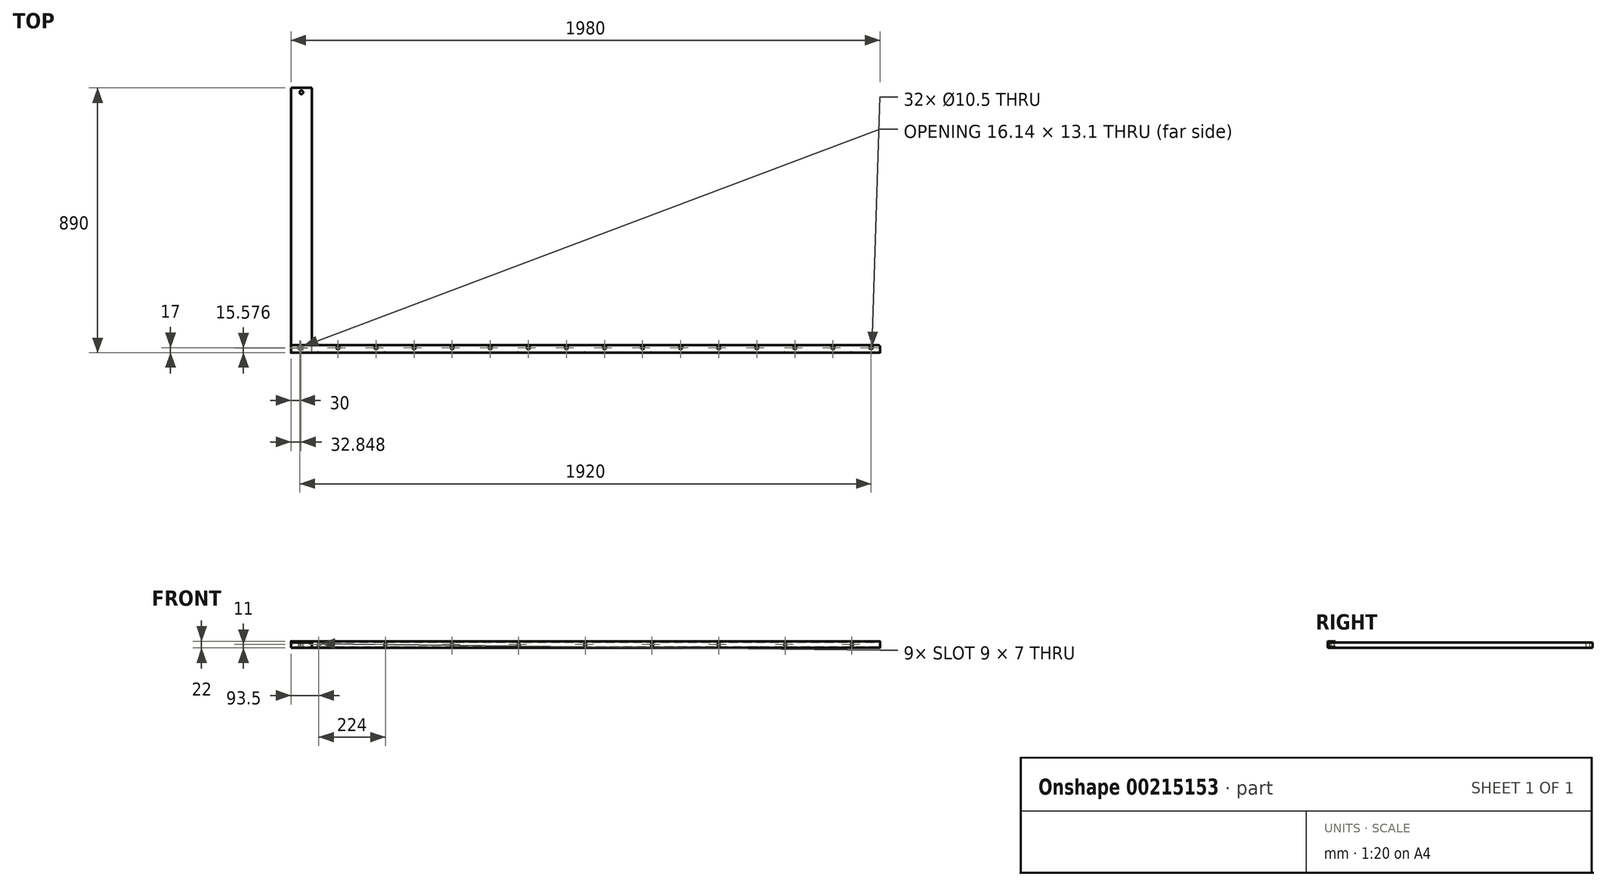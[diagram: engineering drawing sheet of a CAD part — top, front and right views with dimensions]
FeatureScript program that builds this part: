
annotation { "Feature Type Name" : "Feature", "Feature Type Description" : "" }
export const myFeature = defineFeature(function(context is Context, id is Id, definition is map)
    precondition{}
    {
        {
            var Q0;
            Q0=qCreatedBy(makeId("Top.planeOp"),FACE);
            var sketch = newSketch(context, id + "F0", { "sketchPlane" : qUnion([Q0])});
            skLineSegment(sketch, "E0.bottom", {"start": v(0, 0) * mm, "end": v(70, 0) * mm});
            skLineSegment(sketch, "E0.top", {"start": v(0, 890) * mm, "end": v(70, 890) * mm});
            skLineSegment(sketch, "E0.left", {"start": v(0, 0) * mm, "end": v(0, 890) * mm});
            skLineSegment(sketch, "E0.right", {"start": v(70, 0) * mm, "end": v(70, 890) * mm});
            skSolve(sketch);
        }
        {
            var Q0;
            Q0 = qSketchRegion(id + "F0", true);
            extrude(context, id + "F1", {"entities" : qUnion([Q0]), "depth" : 18 * mm});
        }
        {
            var Q0;
            Q0=makeQuery(id+"F1.opExtrude","CAP_FACE",FACE,{"disambiguationData":[OSD([sQuery(id+"F0.wireOp",EDGE,"E0.bottom"),sQuery(id+"F0.wireOp",EDGE,"E0.top"),sQuery(id+"F0.wireOp",EDGE,"E0.left"),sQuery(id+"F0.wireOp",EDGE,"E0.right")])],"isStart":false});
            var sketch = newSketch(context, id + "F2", { "sketchPlane" : qUnion([Q0])});
            skCircle(sketch, "E1", {"center": v(35, 875) * mm, "radius": 6 * mm});
            skCircle(sketch, "E2", {"center": v(35, 15) * mm, "radius": 6 * mm});
            skSolve(sketch);
        }
        {
            var Q0;
            Q0 = qSketchRegion(id + "F2", true);
            extrude(context, id + "F3", {"entities" : qUnion([Q0]), "operationType" : NewBodyOperationType.REMOVE, "endBound" : BoundingType.UP_TO_NEXT, "oppositeDirection" : true, "depth" : 25 * mm});
        }
        {
            var Q0;
            Q0=qCreatedBy(makeId("Right.planeOp"),FACE);
            var sketch = newSketch(context, id + "F4", { "sketchPlane" : qUnion([Q0])});
            skLineSegment(sketch, "E3.bottom", {"start": v(0, 0) * mm, "end": v(25, 0) * mm});
            skLineSegment(sketch, "E3.top", {"start": v(0, 22) * mm, "end": v(25, 22) * mm});
            skLineSegment(sketch, "E3.left", {"start": v(0, 0) * mm, "end": v(0, 22) * mm});
            skLineSegment(sketch, "E3.right", {"start": v(25, 0) * mm, "end": v(25, 22) * mm});
            skSolve(sketch);
        }
        {
            var Q0;
            Q0 = qSketchRegion(id + "F4", true);
            extrude(context, id + "F5", {"entities" : qUnion([Q0]), "depth" : 1980 * mm});
        }
        {
            var Q0;
            Q0=makeQuery(id+"F5.opExtrude","CAP_EDGE",EDGE,{"disambiguationData":[OSD([sQuery(id+"F4.wireOp",EDGE,"E3.right")])],"isStart":true});
            var Q1;
            Q1=makeQuery(id+"F5.opExtrude","CAP_EDGE",EDGE,{"disambiguationData":[OSD([sQuery(id+"F4.wireOp",EDGE,"E3.right")])],"isStart":false});
            fillet(context, id + "F6", {"entities" : qUnion([Q0, Q1]), "radius" : 5 * mm, "tangentPropagation" : true, "allowEdgeOverflow" : false});
        }
        {
            var Q0;
            Q0=makeQuery(id+"F5.opExtrude","SWEPT_EDGE",EDGE,{"disambiguationData":[OSD([sQuery(id+"F4.wireOp",EDGE,"E3.top"),sQuery(id+"F4.wireOp",EDGE,"E3.left")])]});
            var Q1;
            Q1=makeQuery(id+"F5.opExtrude","SWEPT_EDGE",EDGE,{"disambiguationData":[OSD([sQuery(id+"F4.wireOp",EDGE,"E3.bottom"),sQuery(id+"F4.wireOp",EDGE,"E3.left")])]});
            fillet(context, id + "F7", {"entities" : qUnion([Q0, Q1]), "radius" : 2 * mm, "tangentPropagation" : true, "allowEdgeOverflow" : false});
        }
        {
            var Q0;
            Q0=makeQuery(id+"F5.opExtrude","SWEPT_FACE",FACE,{"disambiguationData":[OSD([sQuery(id+"F4.wireOp",EDGE,"E3.right")])]});
            var Q1;
            {var subQ0=sQuery(id+"F4.wireOp",EDGE,"E3.right");Q1=makeQuery(id+"F6.opFillet","BLEND_FACE",FACE,{"disambiguationData":[OSD([subQ0]),TDD([makeQuery(id+"F5.opExtrude","CAP_EDGE",EDGE,{"disambiguationData":[OSD([subQ0])],"isStart":true})])]});}
            var Q2;
            Q2=makeQuery(id+"F5.opExtrude","CAP_FACE",FACE,{"disambiguationData":[OSD([sQuery(id+"F4.wireOp",EDGE,"E3.bottom"),sQuery(id+"F4.wireOp",EDGE,"E3.top"),sQuery(id+"F4.wireOp",EDGE,"E3.left"),sQuery(id+"F4.wireOp",EDGE,"E3.right")])],"isStart":true});
            var Q3;
            {var subQ0=sQuery(id+"F4.wireOp",EDGE,"E3.right");Q3=makeQuery(id+"F6.opFillet","BLEND_FACE",FACE,{"disambiguationData":[OSD([subQ0]),TDD([makeQuery(id+"F5.opExtrude","CAP_EDGE",EDGE,{"disambiguationData":[OSD([subQ0])],"isStart":false})])]});}
            var Q4;
            Q4=makeQuery(id+"F5.opExtrude","CAP_FACE",FACE,{"disambiguationData":[OSD([sQuery(id+"F4.wireOp",EDGE,"E3.bottom"),sQuery(id+"F4.wireOp",EDGE,"E3.top"),sQuery(id+"F4.wireOp",EDGE,"E3.left"),sQuery(id+"F4.wireOp",EDGE,"E3.right")])],"isStart":false});
            shell(context, id + "F8", {"entities" : qUnion([Q0, Q1, Q2, Q3, Q4]), "thickness" : 2.5 * mm});
        }
        {
            var Q0;
            Q0=makeQuery(id+"F5.opExtrude","SWEPT_FACE",FACE,{"disambiguationData":[OSD([sQuery(id+"F4.wireOp",EDGE,"E3.bottom")])]});
            var sketch = newSketch(context, id + "F9", { "sketchPlane" : qUnion([Q0])});
            skCircle(sketch, "E4", {"center": v(1950, -17) * mm, "radius": 5.25 * mm});
            skCircle(sketch, "E5.1.0.0", {"center": v(1822, -17) * mm, "radius": 5.25 * mm});
            skCircle(sketch, "E5.2.0.0", {"center": v(1694, -17) * mm, "radius": 5.25 * mm});
            skCircle(sketch, "E5.3.0.0", {"center": v(1566, -17) * mm, "radius": 5.25 * mm});
            skCircle(sketch, "E5.4.0.0", {"center": v(1438, -17) * mm, "radius": 5.25 * mm});
            skCircle(sketch, "E5.5.0.0", {"center": v(1310, -17) * mm, "radius": 5.25 * mm});
            skCircle(sketch, "E5.6.0.0", {"center": v(1182, -17) * mm, "radius": 5.25 * mm});
            skCircle(sketch, "E5.7.0.0", {"center": v(1054, -17) * mm, "radius": 5.25 * mm});
            skCircle(sketch, "E5.8.0.0", {"center": v(926, -17) * mm, "radius": 5.25 * mm});
            skCircle(sketch, "E5.9.0.0", {"center": v(798, -17) * mm, "radius": 5.25 * mm});
            skCircle(sketch, "E5.10.0.0", {"center": v(670, -17) * mm, "radius": 5.25 * mm});
            skCircle(sketch, "E5.11.0.0", {"center": v(542, -17) * mm, "radius": 5.25 * mm});
            skCircle(sketch, "E5.12.0.0", {"center": v(414, -17) * mm, "radius": 5.25 * mm});
            skCircle(sketch, "E5.13.0.0", {"center": v(286, -17) * mm, "radius": 5.25 * mm});
            skCircle(sketch, "E5.14.0.0", {"center": v(158, -17) * mm, "radius": 5.25 * mm});
            skCircle(sketch, "E5.15.0.0", {"center": v(30, -17) * mm, "radius": 5.25 * mm});
            skLineSegment(sketch, "E5.direction1", {"start": v(1950, -17) * mm, "end": v(1822, -17) * mm, "construction": true});
            skSolve(sketch);
        }
        {
            var Q0;
            Q0 = qSketchRegion(id + "F9", true);
            extrude(context, id + "F10", {"entities" : qUnion([Q0]), "operationType" : NewBodyOperationType.REMOVE, "endBound" : BoundingType.THROUGH_ALL, "oppositeDirection" : true, "depth" : 25 * mm});
        }
        {
            var Q0;
            Q0=makeQuery(id+"F8.opShell","OFFSET_FACE",FACE,{"disambiguationData":[OSD([sQuery(id+"F4.wireOp",EDGE,"E3.left")])]});
            var sketch = newSketch(context, id + "F11", { "sketchPlane" : qUnion([Q0])});
            skLineSegment(sketch, "E6.bottom", {"start": v(-1884.5, 14.5) * mm, "end": v(-1886.5, 14.5) * mm});
            skLineSegment(sketch, "E6.top", {"start": v(-1884.5, 7.5) * mm, "end": v(-1886.5, 7.5) * mm});
            skArc(sketch, "E7", {"start": v(-1884.5, 14.5) * mm, "mid": v(-1881, 11) * mm, "end": v(-1884.5, 7.5) * mm});
            skArc(sketch, "E8", {"start": v(-1886.5, 7.5) * mm, "mid": v(-1890, 11) * mm, "end": v(-1886.5, 14.5) * mm});
            skLineSegment(sketch, "E9", {"start": v(-1887.7, 11) * mm, "end": v(-1873.3, 11) * mm, "construction": true});
            skLineSegment(sketch, "E10.1.0.0", {"start": v(-1660.5, 14.5) * mm, "end": v(-1662.5, 14.5) * mm});
            skLineSegment(sketch, "E10.1.0.1", {"start": v(-1660.5, 7.5) * mm, "end": v(-1662.5, 7.5) * mm});
            skArc(sketch, "E10.1.0.2", {"start": v(-1662.5, 7.5) * mm, "mid": v(-1666, 11) * mm, "end": v(-1662.5, 14.5) * mm});
            skArc(sketch, "E10.1.0.3", {"start": v(-1660.5, 14.5) * mm, "mid": v(-1657, 11) * mm, "end": v(-1660.5, 7.5) * mm});
            skLineSegment(sketch, "E10.2.0.0", {"start": v(-1436.5, 14.5) * mm, "end": v(-1438.5, 14.5) * mm});
            skLineSegment(sketch, "E10.2.0.1", {"start": v(-1436.5, 7.5) * mm, "end": v(-1438.5, 7.5) * mm});
            skArc(sketch, "E10.2.0.2", {"start": v(-1438.5, 7.5) * mm, "mid": v(-1442, 11) * mm, "end": v(-1438.5, 14.5) * mm});
            skArc(sketch, "E10.2.0.3", {"start": v(-1436.5, 14.5) * mm, "mid": v(-1433, 11) * mm, "end": v(-1436.5, 7.5) * mm});
            skLineSegment(sketch, "E10.3.0.0", {"start": v(-1212.5, 14.5) * mm, "end": v(-1214.5, 14.5) * mm});
            skLineSegment(sketch, "E10.3.0.1", {"start": v(-1212.5, 7.5) * mm, "end": v(-1214.5, 7.5) * mm});
            skArc(sketch, "E10.3.0.2", {"start": v(-1214.5, 7.5) * mm, "mid": v(-1218, 11) * mm, "end": v(-1214.5, 14.5) * mm});
            skArc(sketch, "E10.3.0.3", {"start": v(-1212.5, 14.5) * mm, "mid": v(-1209, 11) * mm, "end": v(-1212.5, 7.5) * mm});
            skLineSegment(sketch, "E10.4.0.0", {"start": v(-988.5, 14.5) * mm, "end": v(-990.5, 14.5) * mm});
            skLineSegment(sketch, "E10.4.0.1", {"start": v(-988.5, 7.5) * mm, "end": v(-990.5, 7.5) * mm});
            skArc(sketch, "E10.4.0.2", {"start": v(-990.5, 7.5) * mm, "mid": v(-994, 11) * mm, "end": v(-990.5, 14.5) * mm});
            skArc(sketch, "E10.4.0.3", {"start": v(-988.5, 14.5) * mm, "mid": v(-985, 11) * mm, "end": v(-988.5, 7.5) * mm});
            skLineSegment(sketch, "E10.5.0.0", {"start": v(-764.5, 14.5) * mm, "end": v(-766.5, 14.5) * mm});
            skLineSegment(sketch, "E10.5.0.1", {"start": v(-764.5, 7.5) * mm, "end": v(-766.5, 7.5) * mm});
            skArc(sketch, "E10.5.0.2", {"start": v(-766.5, 7.5) * mm, "mid": v(-770, 11) * mm, "end": v(-766.5, 14.5) * mm});
            skArc(sketch, "E10.5.0.3", {"start": v(-764.5, 14.5) * mm, "mid": v(-761, 11) * mm, "end": v(-764.5, 7.5) * mm});
            skLineSegment(sketch, "E10.6.0.0", {"start": v(-540.5, 14.5) * mm, "end": v(-542.5, 14.5) * mm});
            skLineSegment(sketch, "E10.6.0.1", {"start": v(-540.5, 7.5) * mm, "end": v(-542.5, 7.5) * mm});
            skArc(sketch, "E10.6.0.2", {"start": v(-542.5, 7.5) * mm, "mid": v(-546, 11) * mm, "end": v(-542.5, 14.5) * mm});
            skArc(sketch, "E10.6.0.3", {"start": v(-540.5, 14.5) * mm, "mid": v(-537, 11) * mm, "end": v(-540.5, 7.5) * mm});
            skLineSegment(sketch, "E10.7.0.0", {"start": v(-316.5, 14.5) * mm, "end": v(-318.5, 14.5) * mm});
            skLineSegment(sketch, "E10.7.0.1", {"start": v(-316.5, 7.5) * mm, "end": v(-318.5, 7.5) * mm});
            skArc(sketch, "E10.7.0.2", {"start": v(-318.5, 7.5) * mm, "mid": v(-322, 11) * mm, "end": v(-318.5, 14.5) * mm});
            skArc(sketch, "E10.7.0.3", {"start": v(-316.5, 14.5) * mm, "mid": v(-313, 11) * mm, "end": v(-316.5, 7.5) * mm});
            skLineSegment(sketch, "E10.8.0.0", {"start": v(-92.5, 14.5) * mm, "end": v(-94.5, 14.5) * mm});
            skLineSegment(sketch, "E10.8.0.1", {"start": v(-92.5, 7.5) * mm, "end": v(-94.5, 7.5) * mm});
            skArc(sketch, "E10.8.0.2", {"start": v(-94.5, 7.5) * mm, "mid": v(-98, 11) * mm, "end": v(-94.5, 14.5) * mm});
            skArc(sketch, "E10.8.0.3", {"start": v(-92.5, 14.5) * mm, "mid": v(-89, 11) * mm, "end": v(-92.5, 7.5) * mm});
            skLineSegment(sketch, "E10.direction1", {"start": v(-1886.5, 7.5) * mm, "end": v(-1662.5, 7.5) * mm, "construction": true});
            skSolve(sketch);
        }
        {
            var Q0;
            Q0 = qSketchRegion(id + "F11", true);
            extrude(context, id + "F12", {"entities" : qUnion([Q0]), "operationType" : NewBodyOperationType.REMOVE, "endBound" : BoundingType.UP_TO_NEXT, "oppositeDirection" : true, "depth" : 25 * mm});
        }
    });
